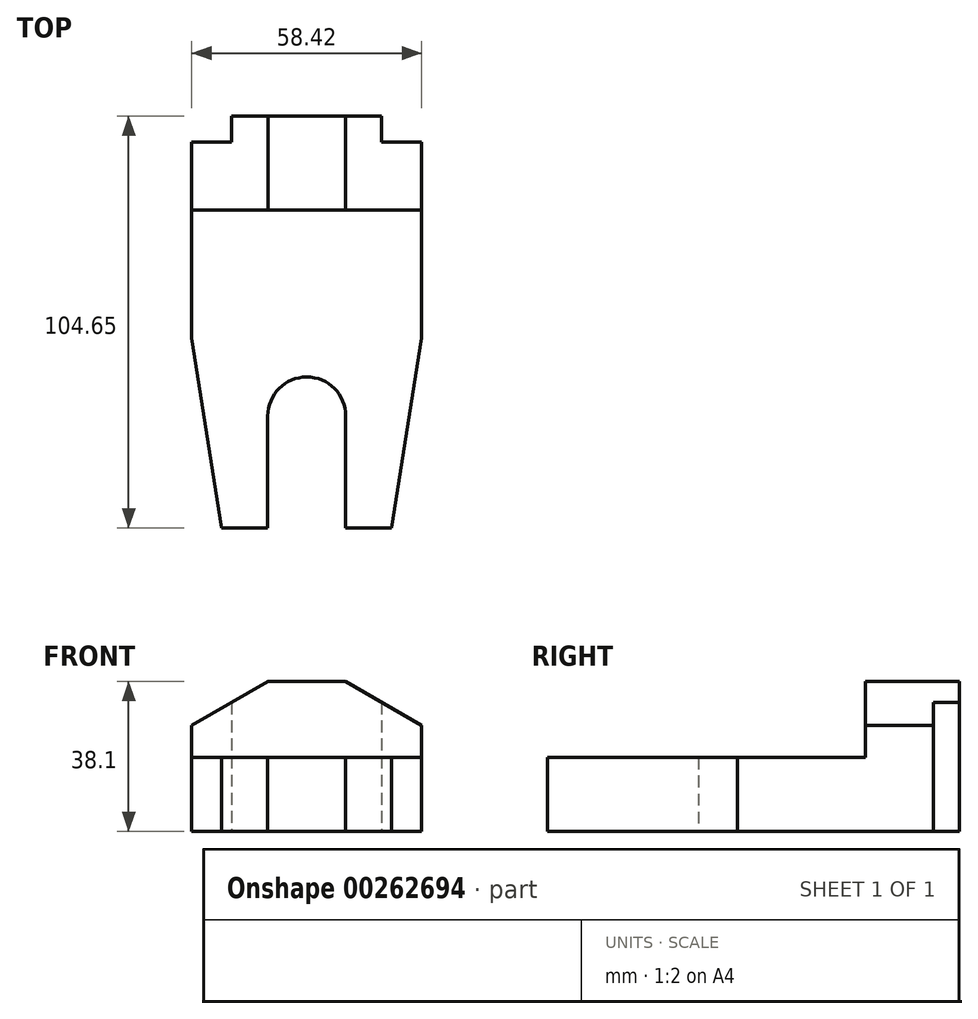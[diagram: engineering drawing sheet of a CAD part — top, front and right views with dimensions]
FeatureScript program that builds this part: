
annotation { "Feature Type Name" : "Feature", "Feature Type Description" : "" }
export const myFeature = defineFeature(function(context is Context, id is Id, definition is map)
    precondition{}
    {
        {
            var Q0;
            Q0=qCreatedBy(makeId("Top.planeOp"),FACE);
            var sketch = newSketch(context, id + "F0", { "sketchPlane" : qUnion([Q0])});
            skLineSegment(sketch, "E0.bottom", {"start": v(16.53, 32.66) * mm, "end": v(-21.57, 32.66) * mm});
            skLineSegment(sketch, "E0.top", {"start": v(19.07, -72) * mm, "end": v(7.39, -72) * mm});
            skLineSegment(sketch, "E0.left", {"start": v(26.69, 26.05) * mm, "end": v(26.69, -23.73) * mm});
            skLineSegment(sketch, "E0.right", {"start": v(-31.73, 26.05) * mm, "end": v(-31.73, -23.73) * mm});
            skLineSegment(sketch, "E1.top", {"start": v(26.69, 26.05) * mm, "end": v(16.53, 26.05) * mm});
            skLineSegment(sketch, "E1.right", {"start": v(16.53, 32.66) * mm, "end": v(16.53, 26.05) * mm});
            skLineSegment(sketch, "E2.top", {"start": v(-31.73, 26.05) * mm, "end": v(-21.57, 26.05) * mm});
            skLineSegment(sketch, "E2.right", {"start": v(-21.57, 32.66) * mm, "end": v(-21.57, 26.05) * mm});
            skLineSegment(sketch, "E3.top", {"start": v(7.39, -43.54) * mm, "end": v(7.39, -43.54) * mm});
            skLineSegment(sketch, "E3.left", {"start": v(7.39, -72) * mm, "end": v(7.39, -43.54) * mm});
            skLineSegment(sketch, "E3.right", {"start": v(-12.43, -72) * mm, "end": v(-12.43, -43.54) * mm});
            skArc(sketch, "E4", {"start": v(7.39, -43.54) * mm, "mid": v(-2.52, -33.64) * mm, "end": v(-12.43, -43.54) * mm});
            skLineSegment(sketch, "E5.trimOffspring", {"start": v(-12.43, -43.54) * mm, "end": v(-12.43, -43.54) * mm});
            skLineSegment(sketch, "E6", {"start": v(-24.11, -72) * mm, "end": v(-31.73, -23.73) * mm});
            skLineSegment(sketch, "E7", {"start": v(19.07, -72) * mm, "end": v(26.69, -23.73) * mm});
            skLineSegment(sketch, "E8.trimOffspring", {"start": v(-12.43, -72) * mm, "end": v(-24.11, -72) * mm});
            skSolve(sketch);
        }
        {
            var Q0;
            Q0 = qSketchRegion(id + "F0", true);
            extrude(context, id + "F1", {"entities" : qUnion([Q0]), "depth" : 38.1 * mm});
        }
        {
            var Q0;
            Q0=qCreatedBy(makeId("Right.planeOp"),FACE);
            var sketch = newSketch(context, id + "F2", { "sketchPlane" : qUnion([Q0])});
            skLineSegment(sketch, "E9.bottom", {"start": v(8.78, 60.4) * mm, "end": v(-126.62, 60.4) * mm});
            skLineSegment(sketch, "E9.top", {"start": v(8.78, 18.8) * mm, "end": v(-126.62, 18.8) * mm});
            skLineSegment(sketch, "E9.left", {"start": v(8.78, 60.4) * mm, "end": v(8.78, 18.8) * mm});
            skLineSegment(sketch, "E9.right", {"start": v(-126.62, 60.4) * mm, "end": v(-126.62, 18.8) * mm});
            skSolve(sketch);
        }
        {
            var Q0;
            Q0 = qSketchRegion(id + "F2", true);
            extrude(context, id + "F3", {"entities" : qUnion([Q0]), "operationType" : NewBodyOperationType.REMOVE, "endBound" : BoundingType.SYMMETRIC, "oppositeDirection" : true, "depth" : 101.6 * mm});
        }
        {
            var Q0;
            Q0=qCreatedBy(makeId("Front.planeOp"),FACE);
            var sketch = newSketch(context, id + "F4", { "sketchPlane" : qUnion([Q0])});
            skLineSegment(sketch, "E10.bottom", {"start": v(26.69, 38.1) * mm, "end": v(-31.73, 38.1) * mm});
            skLineSegment(sketch, "E10.left", {"start": v(26.69, 38.1) * mm, "end": v(26.69, 26.92) * mm});
            skLineSegment(sketch, "E10.right", {"start": v(-31.73, 38.1) * mm, "end": v(-31.73, 26.92) * mm});
            skLineSegment(sketch, "E11", {"start": v(-31.73, 26.92) * mm, "end": v(-12.37, 38.1) * mm});
            skLineSegment(sketch, "E12", {"start": v(26.69, 26.92) * mm, "end": v(7.33, 38.1) * mm});
            skSolve(sketch);
        }
        {
            var Q0;
            Q0 = qSketchRegion(id + "F4", true);
            extrude(context, id + "F5", {"entities" : qUnion([Q0]), "operationType" : NewBodyOperationType.REMOVE, "oppositeDirection" : true, "depth" : 101.6 * mm});
        }
    });
